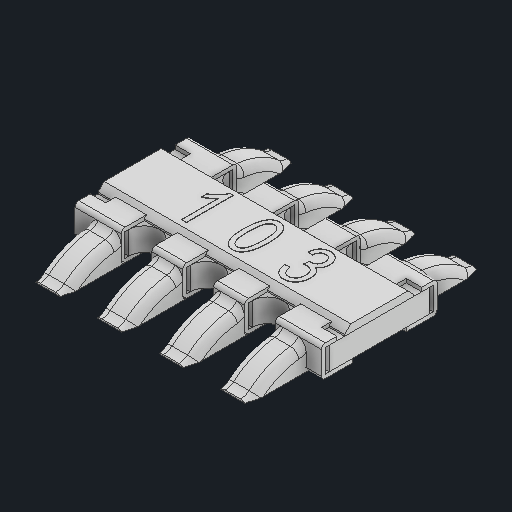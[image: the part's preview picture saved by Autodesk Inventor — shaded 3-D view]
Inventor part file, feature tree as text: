
AUTODESK INVENTOR PART (.ipt)
format: ipt  version: 2023 (Build 270158000, 158)  size: 517,632 bytes
history: native  units: in
note: dims shown in document units (in); Inventor stores cm internally (conversion verified against a paired STEP export)
features: other x8, fillet x2
ambient origin geometry x8: Origin, YZ Plane, XZ Plane, XY Plane, X Axis, Y Axis, Z Axis, Center Point
bodies: Solid1 (feature_tree), Solid2 (feature_tree), Solid3 (feature_tree), Solid4 (feature_tree), Solid5 (feature_tree), Solid6 (feature_tree), Solid7 (feature_tree), Solid8 (feature_tree), Solid9 (feature_tree), Solid10 (feature_tree)
feature tree (10):
  other  "Cut-Extrude7"
  other  "Boss-Extrude5"
  fillet  "Fillet2"  [1 undecoded]
  fillet  "Fillet1"  [1 undecoded]
  other  "LPattern3[1]"
  other  "LPattern3[2]"
  other  "LPattern3[3]"
  other  "LPattern3[4]"
  other  "LPattern3[5]"
  other  "LPattern3[6]"
note: 2 required parameter values undecoded (feature->parameter linkage not recoverable at this tier; creation-order binding heuristic only, values carry confidence <= 0.55)
